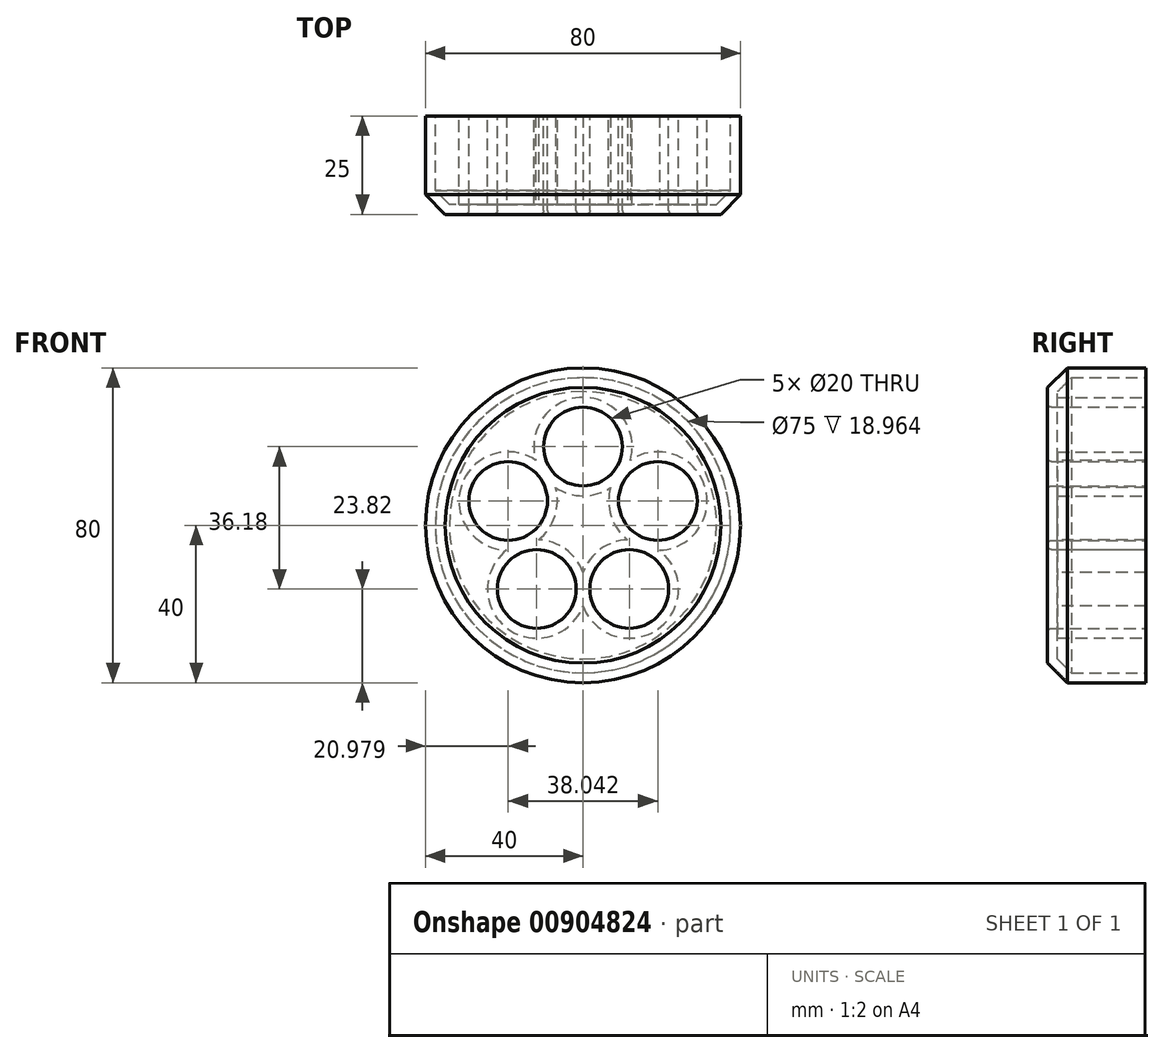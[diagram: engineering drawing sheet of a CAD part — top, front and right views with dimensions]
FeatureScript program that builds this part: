
annotation { "Feature Type Name" : "Feature", "Feature Type Description" : "" }
export const myFeature = defineFeature(function(context is Context, id is Id, definition is map)
    precondition{}
    {
        {
            var Q0;
            Q0=qCreatedBy(makeId("Front.planeOp"),FACE);
            var sketch = newSketch(context, id + "F0", { "sketchPlane" : qUnion([Q0])});
            skCircle(sketch, "E0", {"center": v(0, 0) * mm, "radius": 40 * mm});
            skCircle(sketch, "E1", {"center": v(0, 20) * mm, "radius": 10 * mm});
            skCircle(sketch, "E2.1.0", {"center": v(-19.02, 6.18) * mm, "radius": 10 * mm});
            skCircle(sketch, "E2.2.0", {"center": v(-11.76, -16.18) * mm, "radius": 10 * mm});
            skCircle(sketch, "E3.1.3.0", {"center": v(11.76, -16.18) * mm, "radius": 10 * mm});
            skCircle(sketch, "E3.1.4.0", {"center": v(19.02, 6.18) * mm, "radius": 10 * mm});
            skSolve(sketch);
        }
        {
            var Q0;
            Q0=makeQuery(id+"F0.imprint","IMPRINT",FACE,{"disambiguationData":[TD([[makeQuery(id+"F0.imprint","IMPRINT",EDGE,{"derivedFrom":sQuery(id+"F0.wireOp",EDGE,"E0")}),1.0]])]});
            extrude(context, id + "F1", {"entities" : qUnion([Q0]), "depth" : 25 * mm, "offsetDistance" : 25 * mm});
        }
        {
            var Q0;
            Q0=makeQuery(id+"F1.opExtrude","CAP_EDGE",EDGE,{"disambiguationData":[OSD([sQuery(id+"F0.wireOp",EDGE,"E1")])],"isStart":false});
            var Q1;
            Q1=makeQuery(id+"F1.opExtrude","CAP_EDGE",EDGE,{"disambiguationData":[OSD([sQuery(id+"F0.wireOp",EDGE,"E2.1.0")])],"isStart":false});
            var Q2;
            Q2=makeQuery(id+"F1.opExtrude","CAP_EDGE",EDGE,{"disambiguationData":[OSD([sQuery(id+"F0.wireOp",EDGE,"E2.2.0")])],"isStart":false});
            var Q3;
            Q3=makeQuery(id+"F1.opExtrude","CAP_EDGE",EDGE,{"disambiguationData":[OSD([sQuery(id+"F0.wireOp",EDGE,"E3.1.3.0")])],"isStart":false});
            var Q4;
            Q4=makeQuery(id+"F1.opExtrude","CAP_EDGE",EDGE,{"disambiguationData":[OSD([sQuery(id+"F0.wireOp",EDGE,"E3.1.4.0")])],"isStart":false});
            fillet(context, id + "F2", {"entities" : qUnion([Q0, Q1, Q2, Q3, Q4]), "radius" : 1 * mm, "tangentPropagation" : true, "allowEdgeOverflow" : false});
        }
        {
            var Q0;
            Q0=makeQuery(id+"F1.opExtrude","CAP_EDGE",EDGE,{"disambiguationData":[OSD([sQuery(id+"F0.wireOp",EDGE,"E0")])],"isStart":false});
            chamfer(context, id + "F3", {"entities" : qUnion([Q0]), "width" : 5 * mm, "tangentPropagation" : true});
        }
        {
            var Q0;
            Q0=makeQuery(id+"F1.opExtrude","CAP_FACE",FACE,{"disambiguationData":[OSD([sQuery(id+"F0.wireOp",EDGE,"E0"),sQuery(id+"F0.wireOp",EDGE,"E1"),sQuery(id+"F0.wireOp",EDGE,"E2.1.0"),sQuery(id+"F0.wireOp",EDGE,"E2.2.0"),sQuery(id+"F0.wireOp",EDGE,"E3.1.3.0"),sQuery(id+"F0.wireOp",EDGE,"E3.1.4.0")])],"isStart":true});
            shell(context, id + "F4", {"entities" : qUnion([Q0]), "thickness" : 2.5 * mm});
        }
    });
